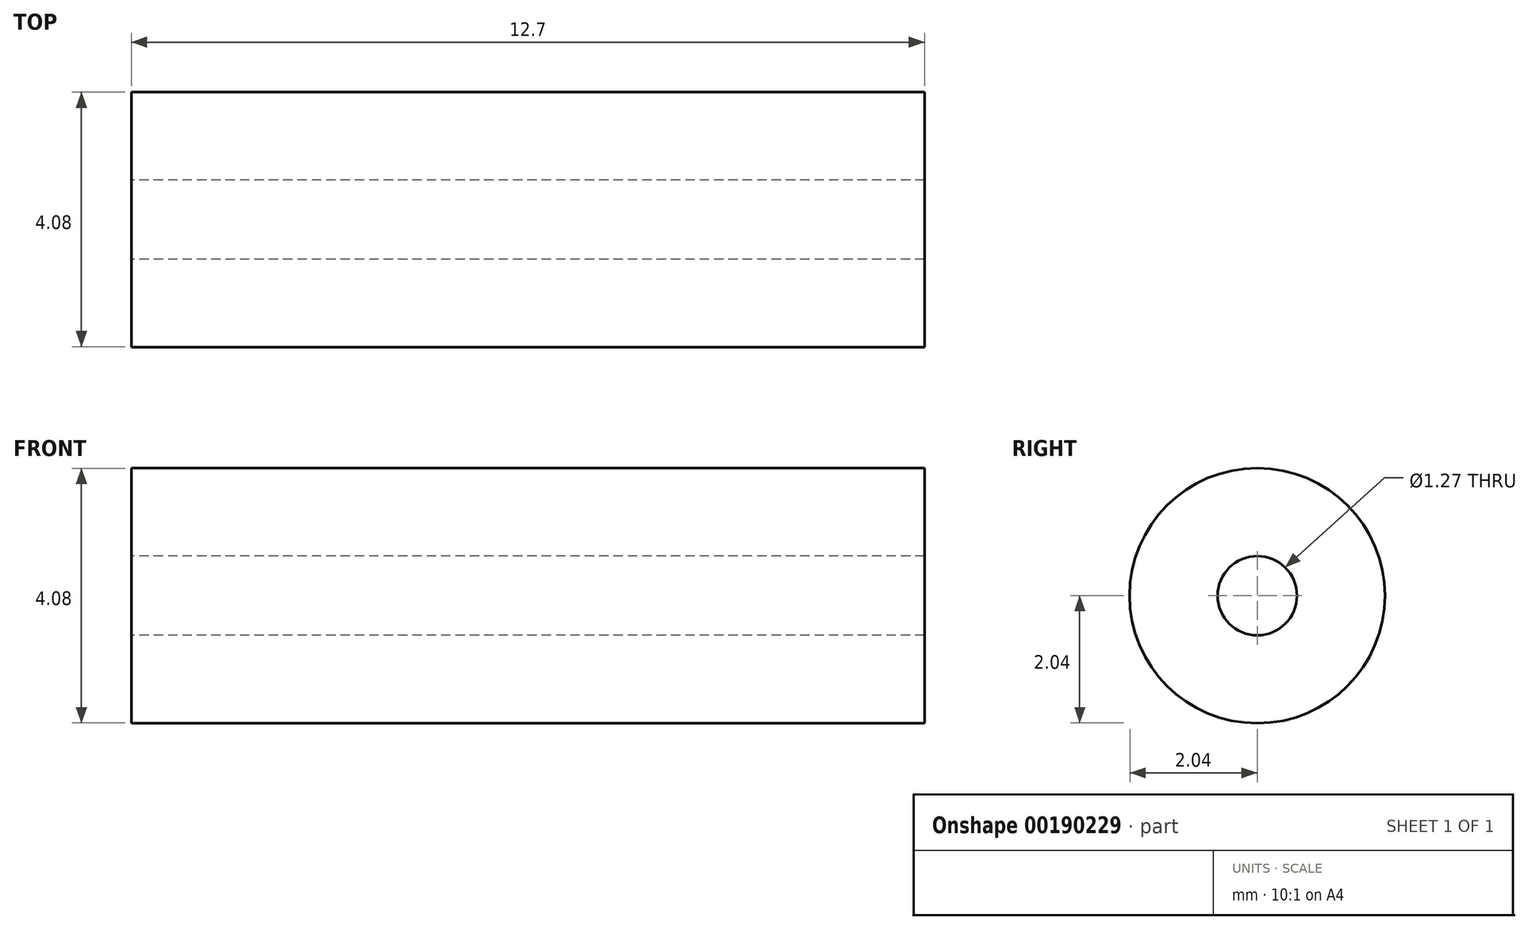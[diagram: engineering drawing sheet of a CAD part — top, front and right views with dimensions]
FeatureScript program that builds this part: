
annotation { "Feature Type Name" : "Feature", "Feature Type Description" : "" }
export const myFeature = defineFeature(function(context is Context, id is Id, definition is map)
    precondition{}
    {
        {
            var Q0;
            Q0=qCreatedBy(makeId("Front.planeOp"),FACE);
            var sketch = newSketch(context, id + "F0", { "sketchPlane" : qUnion([Q0])});
            skLineSegment(sketch, "E0.bottom", {"start": v(0, 0.64) * mm, "end": v(12.7, 0.64) * mm});
            skLineSegment(sketch, "E0.top", {"start": v(0, 2.04) * mm, "end": v(12.7, 2.04) * mm});
            skLineSegment(sketch, "E0.left", {"start": v(0, 0.64) * mm, "end": v(0, 2.04) * mm});
            skLineSegment(sketch, "E0.right", {"start": v(12.7, 0.64) * mm, "end": v(12.7, 2.04) * mm});
            skLineSegment(sketch, "E1", {"start": v(0, 0) * mm, "end": v(12.7, 0) * mm});
            skSolve(sketch);
        }
        {
            var Q0;
            Q0=qSketchRegion(id+"F0",true);
            var Q1;
            Q1=sQuery(id+"F0.wireOp",EDGE,"E1");
            revolve(context, id + "F1", {"entities" : qUnion([Q0]), "axis" : qUnion([Q1]), "revolveType" : RevolveType.FULL});
        }
    });
